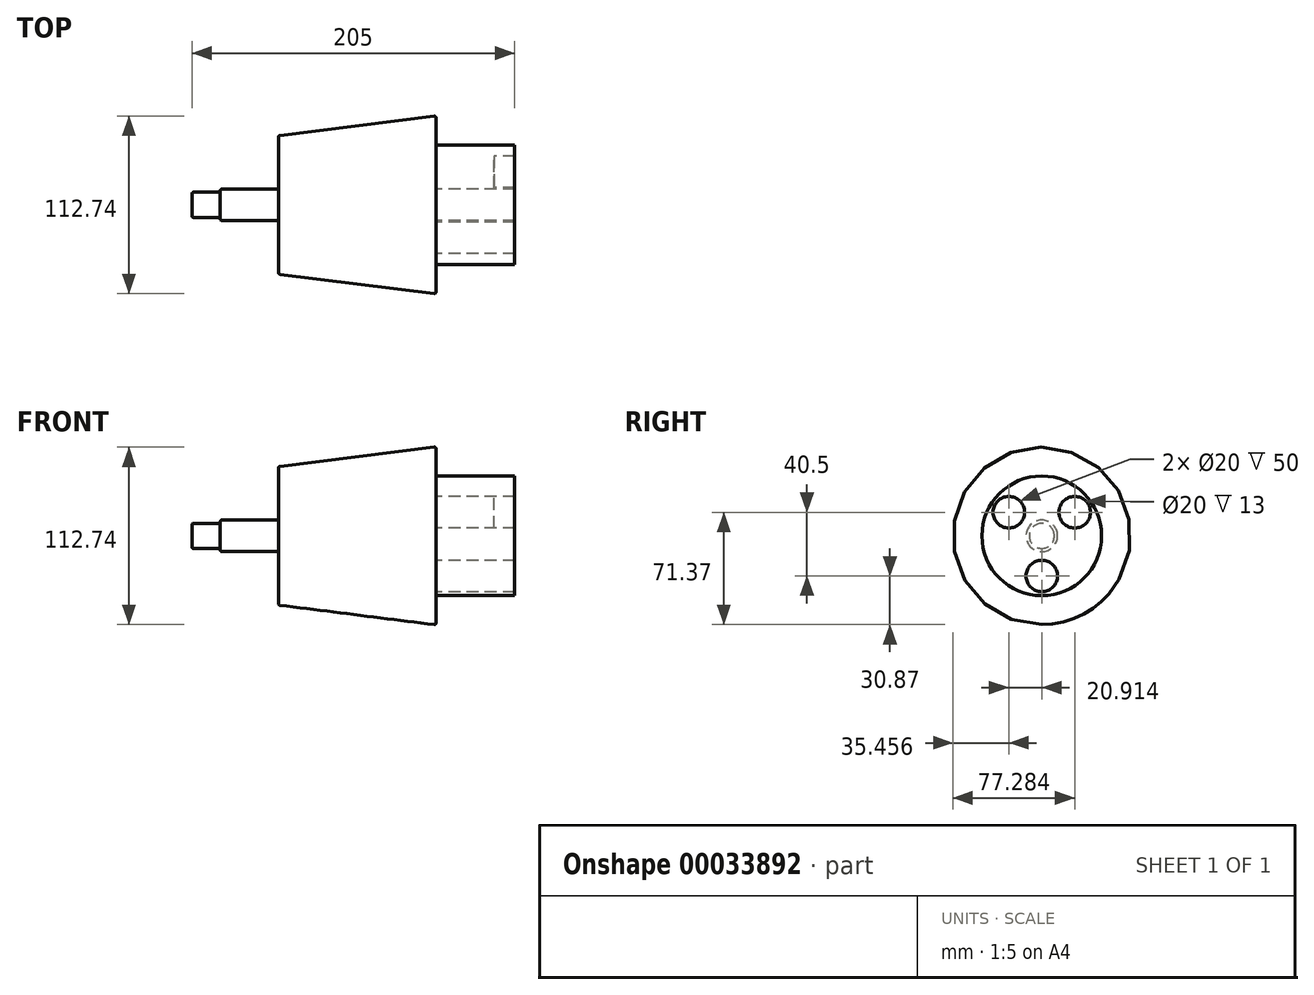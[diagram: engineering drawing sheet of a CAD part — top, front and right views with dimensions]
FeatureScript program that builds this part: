
annotation { "Feature Type Name" : "Feature", "Feature Type Description" : "" }
export const myFeature = defineFeature(function(context is Context, id is Id, definition is map)
    precondition{}
    {
        {
            var Q0;
            Q0=qCreatedBy(makeId("Front.planeOp"),FACE);
            var sketch = newSketch(context, id + "F0", { "sketchPlane" : qUnion([Q0])});
            skLineSegment(sketch, "E0", {"start": v(197.12, 0) * mm, "end": v(-180.58, 0) * mm, "construction": true});
            skLineSegment(sketch, "E1", {"start": v(-114.38, 0) * mm, "end": v(-59.38, 0) * mm});
            skLineSegment(sketch, "E2", {"start": v(-59.38, 0) * mm, "end": v(40.62, 0) * mm});
            skLineSegment(sketch, "E3", {"start": v(40.62, 0) * mm, "end": v(40.62, 56.5) * mm});
            skLineSegment(sketch, "E4", {"start": v(-59.38, 0) * mm, "end": v(-59.38, 44) * mm});
            skLineSegment(sketch, "E5", {"start": v(40.62, 56.5) * mm, "end": v(-59.38, 44) * mm});
            skLineSegment(sketch, "E6", {"start": v(-96.38, 0) * mm, "end": v(-96.38, 10) * mm});
            skLineSegment(sketch, "E7", {"start": v(-114.38, 0) * mm, "end": v(-114.38, 8) * mm});
            skLineSegment(sketch, "E8", {"start": v(-96.38, 10) * mm, "end": v(-59.38, 10) * mm});
            skLineSegment(sketch, "E9", {"start": v(-114.38, 8) * mm, "end": v(-96.38, 8) * mm});
            skSolve(sketch);
        }
        {
            var Q0;
            {var subQ1=sQuery(id+"F0.wireOp",EDGE,"E7");Q0=makeQuery(id+"F0.imprint","IMPRINT",FACE,{"disambiguationData":[TD([[makeQuery(id+"F0.imprint","IMPRINT",EDGE,{"derivedFrom":subQ1}),-1.0]])]});}
            var Q1;
            {var subQ0=sQuery(id+"F0.wireOp",EDGE,"E8");Q1=makeQuery(id+"F0.imprint","IMPRINT",FACE,{"disambiguationData":[TD([[makeQuery(id+"F0.imprint","IMPRINT",EDGE,{"derivedFrom":subQ0}),-1.0]])]});}
            var Q2;
            {var subQ3=sQuery(id+"F0.wireOp",EDGE,"E2");Q2=makeQuery(id+"F0.imprint","IMPRINT",FACE,{"disambiguationData":[TD([[makeQuery(id+"F0.imprint","IMPRINT",EDGE,{"derivedFrom":subQ3}),1.0]])]});}
            var Q3;
            Q3=sQuery(id+"F0.wireOp",EDGE,"E0");
            revolve(context, id + "F1", {"entities" : qUnion([Q0, Q1, Q2]), "axis" : qUnion([Q3]), "revolveType" : RevolveType.FULL});
        }
        {
            var Q0;
            Q0=makeQuery(id+"F1.opRevolve","SWEPT_FACE",FACE,{"disambiguationData":[OSD([sQuery(id+"F0.wireOp",EDGE,"E3")])]});
            var sketch = newSketch(context, id + "F2", { "sketchPlane" : qUnion([Q0])});
            skCircle(sketch, "E10.0", {"center": v(0, 0) * mm, "radius": 56.5 * mm});
            skCircle(sketch, "E11", {"center": v(0, 0) * mm, "radius": 38 * mm});
            skLineSegment(sketch, "E12", {"start": v(0, 38) * mm, "end": v(0, -38) * mm, "construction": true});
            skLineSegment(sketch, "E13", {"start": v(0, 38) * mm, "end": v(0, 35.5) * mm});
            skPoint(sketch, "E14", {"position": v(0, 25.5) * mm});
            skCircle(sketch, "E15", {"center": v(0, 25.5) * mm, "radius": 10 * mm});
            skLineSegment(sketch, "E16", {"start": v(0, 38) * mm, "end": v(0, 15) * mm, "construction": true});
            skLineSegment(sketch, "E17", {"start": v(0, 15) * mm, "end": v(41.83, 15) * mm, "construction": true});
            skLineSegment(sketch, "E18", {"start": v(34.91, 15) * mm, "end": v(30.91, 15) * mm});
            skPoint(sketch, "E19", {"position": v(20.91, 15) * mm});
            skCircle(sketch, "E20", {"center": v(20.91, 15) * mm, "radius": 10 * mm});
            skCircle(sketch, "E21.MirrorC", {"center": v(-20.91, 15) * mm, "radius": 10 * mm});
            skLineSegment(sketch, "E22", {"start": v(28.97, 0) * mm, "end": v(-30.47, 0) * mm, "construction": true});
            skCircle(sketch, "E23.MirrorC", {"center": v(0, -25.5) * mm, "radius": 10 * mm});
            skSolve(sketch);
        }
        {
            var Q0;
            Q0=makeQuery(id+"F2.imprint","IMPRINT",FACE,{"disambiguationData":[TD([[makeQuery(id+"F2.imprint","IMPRINT",EDGE,{"derivedFrom":sQuery(id+"F2.wireOp",EDGE,"E21.MirrorC")}),-1.0]])]});
            var Q1;
            Q1=makeQuery(id+"F2.imprint","IMPRINT",FACE,{"disambiguationData":[TD([[makeQuery(id+"F2.imprint","IMPRINT",EDGE,{"derivedFrom":sQuery(id+"F2.wireOp",EDGE,"E20")}),1.0]])]});
            extrude(context, id + "F3", {"entities" : qUnion([Q0, Q1]), "operationType" : NewBodyOperationType.ADD, "depth" : 37 * mm});
        }
        {
            var Q0;
            Q0=makeQuery(id+"F2.imprint","IMPRINT",FACE,{"disambiguationData":[TD([[makeQuery(id+"F2.imprint","IMPRINT",EDGE,{"derivedFrom":sQuery(id+"F2.wireOp",EDGE,"E15")}),1.0]])]});
            var Q1;
            Q1=makeQuery(id+"F2.imprint","IMPRINT",FACE,{"disambiguationData":[TD([[makeQuery(id+"F2.imprint","IMPRINT",EDGE,{"derivedFrom":sQuery(id+"F2.wireOp",EDGE,"E23.MirrorC")}),-1.0]])]});
            extrude(context, id + "F4", {"entities" : qUnion([Q0, Q1]), "operationType" : NewBodyOperationType.ADD, "depth" : 50 * mm});
        }
        {
            var Q0;
            Q0=makeQuery(id+"F2.imprint","IMPRINT",FACE,{"disambiguationData":[TD([[makeQuery(id+"F2.imprint","IMPRINT",EDGE,{"derivedFrom":sQuery(id+"F2.wireOp",EDGE,"E15")}),-1.0]])]});
            extrude(context, id + "F5", {"entities" : qUnion([Q0]), "operationType" : NewBodyOperationType.ADD, "depth" : 30 * mm});
        }
        {
            var Q0;
            Q0=makeQuery(id+"F1.opRevolve","SWEPT_EDGE",EDGE,{"disambiguationData":[OSD([sQuery(id+"F0.wireOp",EDGE,"E4"),sQuery(id+"F0.wireOp",EDGE,"E5")])]});
            var Q1;
            Q1=makeQuery(id+"F1.opRevolve","SWEPT_EDGE",EDGE,{"disambiguationData":[OSD([sQuery(id+"F0.wireOp",EDGE,"E3"),sQuery(id+"F0.wireOp",EDGE,"E5")])]});
            var Q2;
            Q2=makeQuery(id+"F1.opRevolve","SWEPT_EDGE",EDGE,{"disambiguationData":[OSD([sQuery(id+"F0.wireOp",EDGE,"E6"),sQuery(id+"F0.wireOp",EDGE,"E8")])]});
            var Q3;
            Q3=makeQuery(id+"F1.opRevolve","SWEPT_EDGE",EDGE,{"disambiguationData":[OSD([sQuery(id+"F0.wireOp",EDGE,"E7"),sQuery(id+"F0.wireOp",EDGE,"E9")])]});
            var Q4;
            Q4=makeQuery(id+"F5.opExtrude","CAP_EDGE",EDGE,{"disambiguationData":[OSD([sQuery(id+"F2.wireOp",EDGE,"E11")])],"isStart":false});
            fillet(context, id + "F6", {"entities" : qUnion([Q0, Q1, Q2, Q3, Q4]), "radius" : 1 * mm, "tangentPropagation" : true, "allowEdgeOverflow" : false});
        }
        {
            var Q0;
            Q0=makeQuery(id+"F5.opExtrude","CAP_EDGE",EDGE,{"disambiguationData":[OSD([sQuery(id+"F2.wireOp",EDGE,"E11")])],"isStart":true});
            var Q1;
            Q1=makeQuery(id+"F1.opRevolve","SWEPT_FACE",FACE,{"disambiguationData":[OSD([sQuery(id+"F0.wireOp",EDGE,"E4")])]});
            var Q2;
            Q2=makeQuery(id+"F6.opFillet","BLEND_EDGE",EDGE,{"blendedFrom":[makeQuery(id+"F1.opRevolve","SWEPT_EDGE",EDGE,{"disambiguationData":[OSD([sQuery(id+"F0.wireOp",EDGE,"E6"),sQuery(id+"F0.wireOp",EDGE,"E8")])]}),makeQuery(id+"F1.opRevolve","SWEPT_FACE",FACE,{"disambiguationData":[OSD([sQuery(id+"F0.wireOp",EDGE,"E9")])]})],"blendedInto":[makeQuery(id+"F1.opRevolve","SWEPT_FACE",FACE,{"disambiguationData":[OSD([sQuery(id+"F0.wireOp",EDGE,"E9")])]})]});
            fillet(context, id + "F7", {"entities" : qUnion([Q0, Q1, Q2]), "radius" : 1 * mm, "tangentPropagation" : true, "allowEdgeOverflow" : false});
        }
    });
